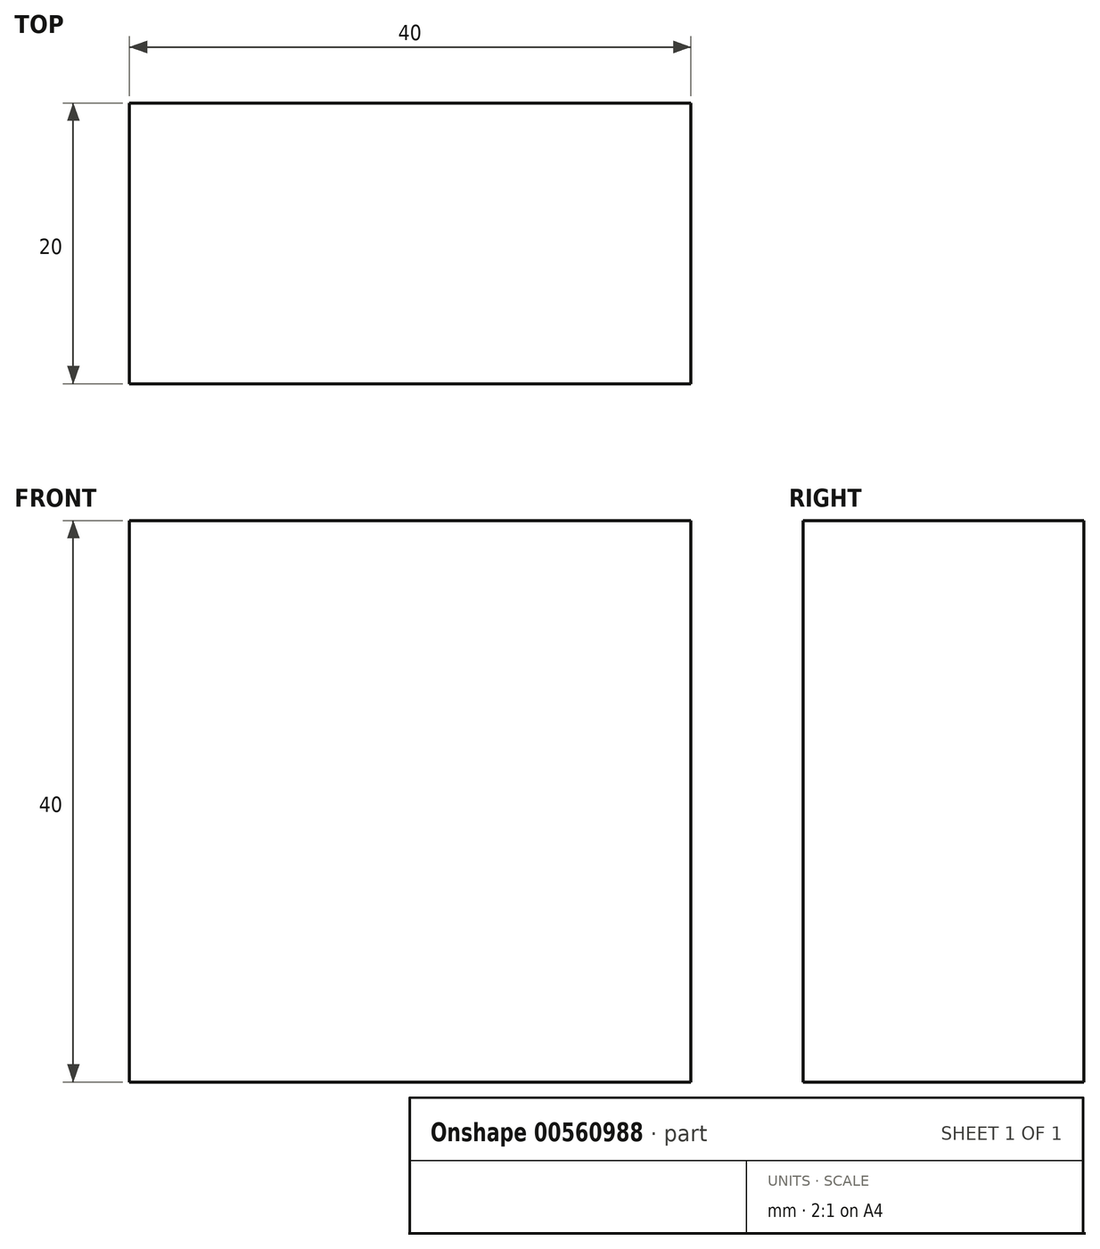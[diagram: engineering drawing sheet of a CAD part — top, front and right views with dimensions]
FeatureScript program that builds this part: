
annotation { "Feature Type Name" : "Feature", "Feature Type Description" : "" }
export const myFeature = defineFeature(function(context is Context, id is Id, definition is map)
    precondition{}
    {
        {
            var Q0;
            Q0=qCreatedBy(makeId("Front.planeOp"),FACE);
            var sketch = newSketch(context, id + "F0", { "sketchPlane" : qUnion([Q0])});
            skLineSegment(sketch, "E0.bottom", {"start": v(20, -20) * mm, "end": v(-20, -20) * mm});
            skLineSegment(sketch, "E0.top", {"start": v(20, 20) * mm, "end": v(-20, 20) * mm});
            skLineSegment(sketch, "E0.left", {"start": v(20, -20) * mm, "end": v(20, 20) * mm});
            skLineSegment(sketch, "E0.right", {"start": v(-20, -20) * mm, "end": v(-20, 20) * mm});
            skPoint(sketch, "E0.middle", {"position": v(0, 0) * mm});
            skSolve(sketch);
        }
        {
            var Q0;
            Q0=qSketchRegion(id+"F0",true);
            extrude(context, id + "F1", {"entities" : qUnion([Q0]), "endBound" : BoundingType.SYMMETRIC, "depth" : 20 * mm});
        }
    });
